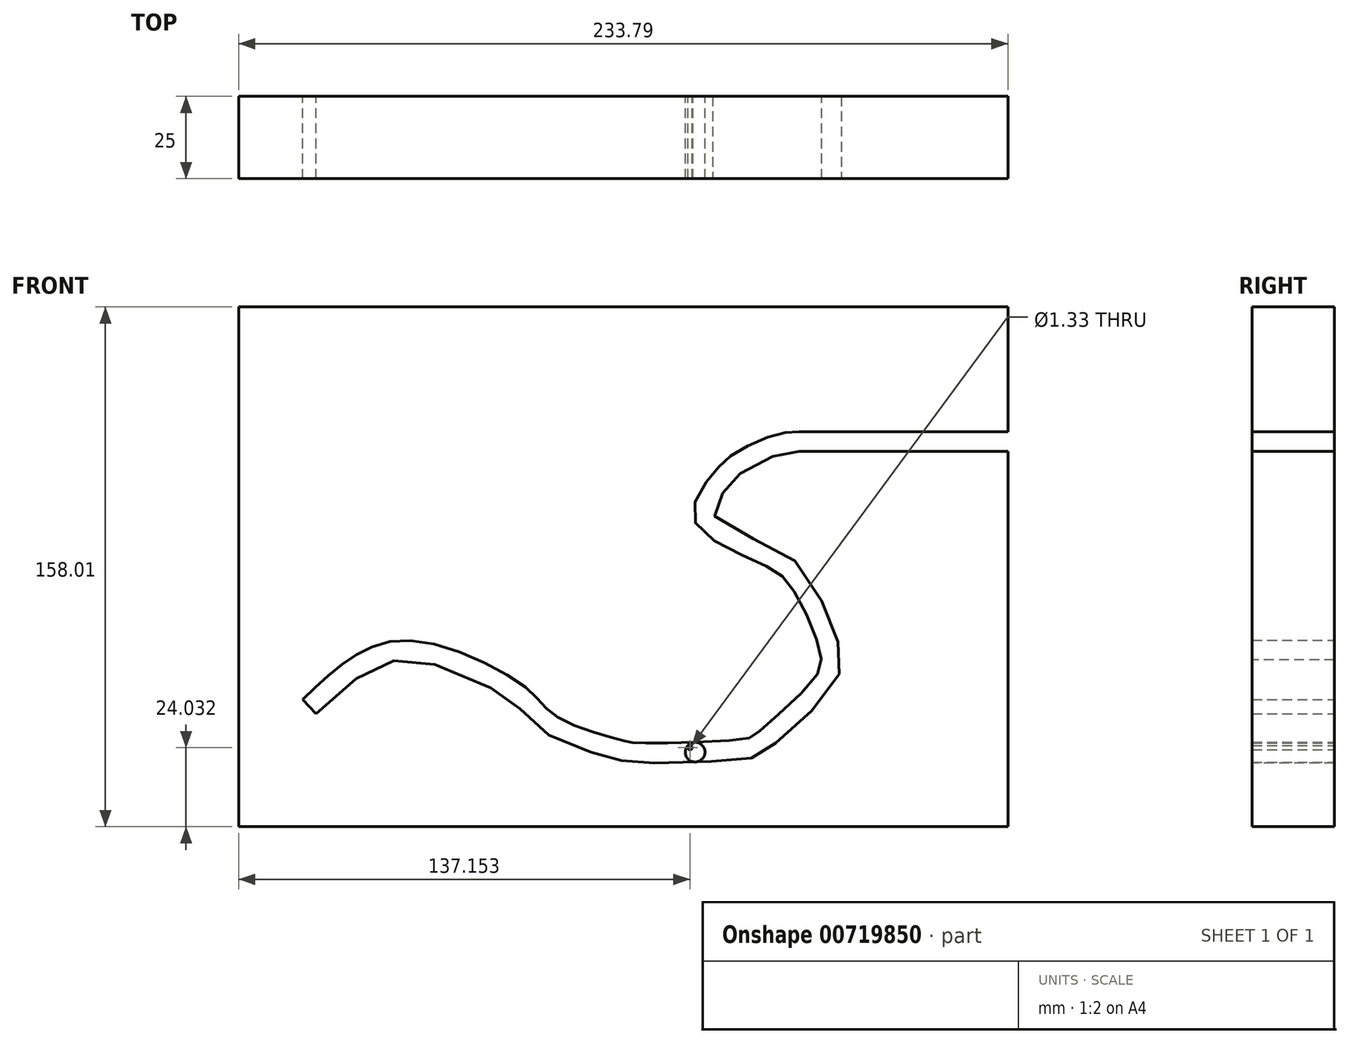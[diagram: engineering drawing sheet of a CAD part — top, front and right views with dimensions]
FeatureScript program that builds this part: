
annotation { "Feature Type Name" : "Feature", "Feature Type Description" : "" }
export const myFeature = defineFeature(function(context is Context, id is Id, definition is map)
    precondition{}
    {
        {
            var Q0;
            Q0=qCreatedBy(makeId("Front.planeOp"),FACE);
            var sketch = newSketch(context, id + "F0", { "sketchPlane" : qUnion([Q0])});
            skFitSpline(sketch, "E0", {"points": [v(0, 0) * mm, v(14.1, 12.11) * mm, v(34.06, 17.81) * mm, v(68.26, 3.28) * mm, v(77.67, -5.56) * mm, v(97.05, -12.4) * mm, v(102.18, -13.25) * mm, v(133.81, -12.11) * mm, v(138.66, -9.83) * mm, v(155.76, 6.7) * mm, v(157.19, 14.96) * mm, v(148.64, 34.06) * mm, v(139.52, 41.18) * mm, v(119, 54.58) * mm, v(124.4, 68.26) * mm, v(130.96, 74.53) * mm, v(143.8, 80.52) * mm, v(150.92, 81.37) * mm], "startDerivative": vector(210.86, 201.52) * mm, "endDerivative": vector(161.32, 0) * mm});
            skFitSpline(sketch, "E1.0", {"points": [v(4.15, -4.34) * mm, v(5.24, -3.29) * mm, v(7.41, -1.22) * mm, v(10.63, 1.75) * mm, v(13.33, 4.04) * mm, v(15.51, 5.74) * mm, v(16.89, 6.75) * mm, v(18, 7.51) * mm, v(19.11, 8.24) * mm, v(20.5, 9.07) * mm, v(22.16, 9.93) * mm, v(24.41, 10.9) * mm, v(26.76, 11.57) * mm, v(29.35, 11.91) * mm, v(31.1, 11.97) * mm, v(32.62, 11.92) * mm, v(33.8, 11.82) * mm, v(35.07, 11.65) * mm, v(36.84, 11.35) * mm, v(39.2, 10.83) * mm, v(42.2, 9.98) * mm, v(45.27, 8.94) * mm, v(49.38, 7.34) * mm, v(53.4, 5.49) * mm, v(57.1, 3.53) * mm, v(59.64, 2.05) * mm, v(61.51, 0.84) * mm, v(62.83, -0.1) * mm, v(63.57, -0.65) * mm, v(64.1, -1.07) * mm, v(64.48, -1.38) * mm, v(64.82, -1.68) * mm, v(65.48, -2.26) * mm, v(66.36, -3.13) * mm, v(67.45, -4.32) * mm, v(68.62, -5.66) * mm, v(70, -7.15) * mm, v(71.43, -8.47) * mm, v(72.77, -9.51) * mm, v(73.87, -10.27) * mm, v(75.07, -11) * mm, v(76.3, -11.67) * mm, v(77.59, -12.3) * mm, v(79.33, -13.07) * mm, v(81.59, -13.96) * mm, v(84.34, -14.93) * mm, v(87.06, -15.8) * mm, v(89.65, -16.58) * mm, v(91.63, -17.13) * mm, v(93.04, -17.52) * mm, v(94, -17.79) * mm, v(94.72, -17.98) * mm, v(95.22, -18.12) * mm, v(95.56, -18.21) * mm, v(95.88, -18.3) * mm, v(96.29, -18.42) * mm, v(96.8, -18.56) * mm, v(97.45, -18.72) * mm, v(98.17, -18.88) * mm, v(98.95, -19.02) * mm, v(99.75, -19.12) * mm, v(100.59, -19.19) * mm, v(101.48, -19.23) * mm, v(102.46, -19.27) * mm, v(103.96, -19.3) * mm, v(106.13, -19.3) * mm, v(109.16, -19.28) * mm, v(112.5, -19.23) * mm, v(116.03, -19.15) * mm, v(119.64, -19.03) * mm, v(123.2, -18.89) * mm, v(126.6, -18.72) * mm, v(129.2, -18.56) * mm, v(131.1, -18.42) * mm, v(132.42, -18.3) * mm, v(133.62, -18.18) * mm, v(134.72, -18.05) * mm, v(135.74, -17.9) * mm, v(136.77, -17.69) * mm, v(137.84, -17.38) * mm, v(138.94, -16.95) * mm, v(139.96, -16.4) * mm, v(140.83, -15.82) * mm, v(141.53, -15.27) * mm, v(142.04, -14.84) * mm, v(142.44, -14.5) * mm, v(142.84, -14.15) * mm, v(143.42, -13.66) * mm, v(144.2, -12.98) * mm, v(145.07, -12.24) * mm, v(146, -11.42) * mm, v(147.32, -10.26) * mm, v(149.1, -8.7) * mm, v(152.06, -5.99) * mm, v(155.06, -3.12) * mm, v(157.78, -0.27) * mm, v(159.62, 1.83) * mm, v(160.94, 3.58) * mm, v(161.86, 5.05) * mm, v(162.48, 6.22) * mm, v(163, 7.46) * mm, v(163.39, 8.77) * mm, v(163.63, 10.12) * mm, v(163.72, 11.45) * mm, v(163.68, 12.73) * mm, v(163.54, 13.94) * mm, v(163.33, 15.09) * mm, v(163.12, 16) * mm, v(162.93, 16.73) * mm, v(162.72, 17.47) * mm, v(162.44, 18.42) * mm, v(162.06, 19.59) * mm, v(161.5, 21.2) * mm, v(160.72, 23.27) * mm, v(159.67, 25.83) * mm, v(158.52, 28.41) * mm, v(157.31, 30.95) * mm, v(156.05, 33.38) * mm, v(154.75, 35.67) * mm, v(153.4, 37.76) * mm, v(152, 39.66) * mm, v(150.4, 41.4) * mm, v(148.65, 42.92) * mm, v(146.77, 44.2) * mm, v(144.8, 45.31) * mm, v(142.73, 46.32) * mm, v(140.44, 47.35) * mm, v(137.97, 48.43) * mm, v(135.42, 49.57) * mm, v(132.88, 50.77) * mm, v(130.46, 52.02) * mm, v(128.3, 53.3) * mm, v(126.82, 54.33) * mm, v(125.9, 55.1) * mm, v(125.35, 55.63) * mm, v(124.96, 56.08) * mm, v(124.73, 56.41) * mm, v(124.66, 56.55) * mm, v(124.65, 56.6) * mm, v(124.64, 56.6) * mm, v(124.64, 56.62) * mm, v(124.63, 56.67) * mm, v(124.62, 56.83) * mm, v(124.64, 57.11) * mm, v(124.75, 57.65) * mm, v(125.08, 58.6) * mm, v(125.8, 59.99) * mm, v(126.6, 61.24) * mm, v(127.33, 62.25) * mm, v(127.9, 63) * mm, v(128.37, 63.62) * mm, v(128.76, 64.1) * mm, v(129.05, 64.45) * mm, v(129.33, 64.8) * mm, v(129.68, 65.23) * mm, v(130.1, 65.74) * mm, v(130.57, 66.27) * mm, v(131.14, 66.91) * mm, v(131.8, 67.59) * mm, v(132.57, 68.28) * mm, v(133.3, 68.85) * mm, v(133.98, 69.33) * mm, v(134.76, 69.85) * mm, v(135.91, 70.55) * mm, v(137.48, 71.42) * mm, v(139.16, 72.27) * mm, v(140.89, 73.07) * mm, v(142.3, 73.66) * mm, v(143.38, 74.08) * mm, v(144.16, 74.35) * mm, v(144.88, 74.59) * mm, v(145.54, 74.78) * mm, v(146.14, 74.93) * mm, v(146.9, 75.1) * mm, v(147.76, 75.23) * mm, v(148.75, 75.33) * mm, v(149.77, 75.37) * mm, v(150.52, 75.37) * mm, v(150.92, 75.37) * mm]});
            skCircle(sketch, "E2", {"center": v(119.3, -16.04) * mm, "radius": 3 * mm});
            skPoint(sketch, "E2.first.point", {"position": v(119.2, -13.04) * mm});
            skPoint(sketch, "E2.second.point", {"position": v(119.41, -19.03) * mm});
            skPoint(sketch, "E2.third.point", {"position": v(122.3, -15.86) * mm});
            skLineSegment(sketch, "E3.bottom", {"start": v(-19.42, 119.3) * mm, "end": v(214.37, 119.3) * mm});
            skLineSegment(sketch, "E3.top", {"start": v(-19.42, -38.7) * mm, "end": v(214.37, -38.7) * mm});
            skLineSegment(sketch, "E3.left", {"start": v(-19.42, 119.3) * mm, "end": v(-19.42, -38.7) * mm});
            skLineSegment(sketch, "E3.right", {"start": v(214.37, 119.3) * mm, "end": v(214.37, -38.7) * mm});
            skLineSegment(sketch, "E4", {"start": v(150.92, 75.37) * mm, "end": v(214.37, 75.37) * mm});
            skLineSegment(sketch, "E5", {"start": v(150.92, 81.37) * mm, "end": v(214.37, 81.37) * mm});
            skLineSegment(sketch, "E6", {"start": v(4.15, -4.34) * mm, "end": v(0, 0) * mm});
            skCircle(sketch, "E7", {"center": v(117.73, -14.67) * mm, "radius": 0.67 * mm});
            skSolve(sketch);
        }
        {
            var Q0;
            {var subQ0=sQuery(id+"F0.wireOp",EDGE,"E2");var subQ1=makeQuery(id+"F0.imprint","INTERSECT",VERTEX,{"derivedFrom":[sQuery(id+"F0.wireOp",EDGE,"E0"),subQ0]});Q0=makeQuery(id+"F0.imprint","IMPRINT",FACE,{"disambiguationData":[TD([[makeQuery(id+"F0.imprint","IMPRINT",EDGE,{"disambiguationData":[TD([[subQ1,-1.0]])],"derivedFrom":subQ0}),1.0]])]});}
            extrude(context, id + "F1", {"entities" : qUnion([Q0]), "depth" : 25 * mm, "offsetDistance" : 25 * mm});
        }
        {
            var Q0;
            {var subQ1=sQuery(id+"F0.wireOp",EDGE,"E3.bottom");Q0=makeQuery(id+"F0.imprint","IMPRINT",FACE,{"disambiguationData":[TD([[makeQuery(id+"F0.imprint","IMPRINT",EDGE,{"derivedFrom":subQ1}),-1.0]])]});}
            extrude(context, id + "F2", {"entities" : qUnion([Q0]), "depth" : 25 * mm, "offsetDistance" : 25 * mm});
        }
    });
